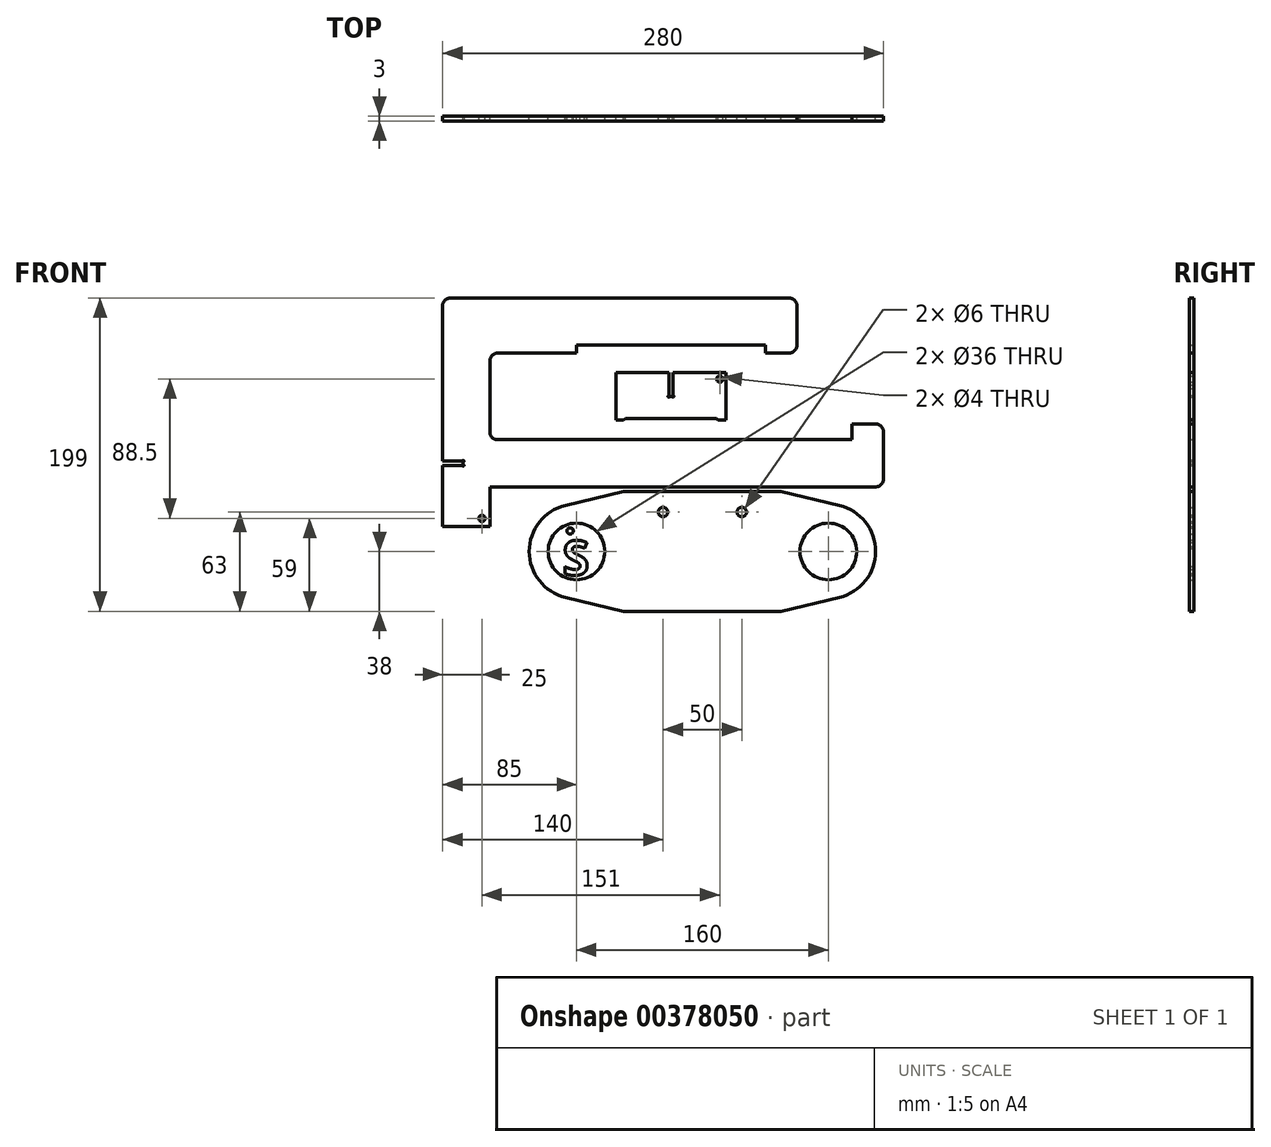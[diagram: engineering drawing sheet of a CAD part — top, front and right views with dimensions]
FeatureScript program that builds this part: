
annotation { "Feature Type Name" : "Feature", "Feature Type Description" : "" }
export const myFeature = defineFeature(function(context is Context, id is Id, definition is map)
    precondition{}
    {
        {
            var Q0;
            Q0=qCreatedBy(makeId("Front.planeOp"),FACE);
            var sketch = newSketch(context, id + "F0", { "sketchPlane" : qUnion([Q0])});
            skLineSegment(sketch, "E0", {"start": v(60, 27.5) * mm, "end": v(80, 27.5) * mm});
            skLineSegment(sketch, "E1", {"start": v(80, 27.5) * mm, "end": v(80, 62.5) * mm});
            skLineSegment(sketch, "E2", {"start": v(80, 62.5) * mm, "end": v(-145, 62.5) * mm});
            skLineSegment(sketch, "E3", {"start": v(-145, 62.5) * mm, "end": v(-145, -57.5) * mm});
            skLineSegment(sketch, "E4", {"start": v(-115, -57.5) * mm, "end": v(135, -57.5) * mm});
            skLineSegment(sketch, "E5", {"start": v(135, -57.5) * mm, "end": v(135, -17.5) * mm});
            skLineSegment(sketch, "E6", {"start": v(135, -17.5) * mm, "end": v(115, -17.5) * mm});
            skLineSegment(sketch, "E7", {"start": v(115, -17.5) * mm, "end": v(115, -27.5) * mm});
            skLineSegment(sketch, "E8", {"start": v(115, -27.5) * mm, "end": v(-115, -27.5) * mm});
            skLineSegment(sketch, "E9", {"start": v(-115, -27.5) * mm, "end": v(-115, 27.5) * mm});
            skLineSegment(sketch, "E10", {"start": v(-115, 27.5) * mm, "end": v(-60, 27.5) * mm});
            skLineSegment(sketch, "E11", {"start": v(-60, 27.5) * mm, "end": v(-60, 32.5) * mm});
            skLineSegment(sketch, "E12", {"start": v(-60, 32.5) * mm, "end": v(60, 32.5) * mm});
            skLineSegment(sketch, "E13", {"start": v(60, 32.5) * mm, "end": v(60, 27.5) * mm});
            skLineSegment(sketch, "E14", {"start": v(0, 32.5) * mm, "end": v(0, -27.5) * mm, "construction": true});
            skPoint(sketch, "E15", {"position": v(0, -27.5) * mm});
            skPoint(sketch, "E16", {"position": v(109.4, 7.93) * mm});
            skPoint(sketch, "E17", {"position": v(-115, 0) * mm});
            skLineSegment(sketch, "E18", {"start": v(-145, -57.5) * mm, "end": v(-145, -82.5) * mm});
            skLineSegment(sketch, "E19", {"start": v(-145, -82.5) * mm, "end": v(-115, -82.5) * mm});
            skLineSegment(sketch, "E20", {"start": v(-115, -82.5) * mm, "end": v(-115, -57.5) * mm});
            skCircle(sketch, "E21", {"center": v(-120, -77.5) * mm, "radius": 2 * mm});
            skSolve(sketch);
        }
        {
            var Q0;
            Q0=makeQuery(id+"F0.imprint","IMPRINT",FACE,{"disambiguationData":[TD([[makeQuery(id+"F0.imprint","IMPRINT",EDGE,{"derivedFrom":sQuery(id+"F0.wireOp",EDGE,"E0")}),1.0]])]});
            extrude(context, id + "F1", {"entities" : qUnion([Q0]), "depth" : 3 * mm, "symmetric" : true});
        }
        {
            var Q0;
            Q0=qCreatedBy(makeId("Front.planeOp"),FACE);
            var sketch = newSketch(context, id + "F2", { "sketchPlane" : qUnion([Q0])});
            skArc(sketch, "E22", {"start": v(-66.96, -69.32) * mm, "mid": v(-83.55, -79.91) * mm, "end": v(-90, -98.5) * mm});
            skArc(sketch, "E23", {"start": v(-42, -98.5) * mm, "mid": v(-60, -80.5) * mm, "end": v(-78, -98.5) * mm});
            skLineSegment(sketch, "E24", {"start": v(-66.96, -69.32) * mm, "end": v(-30, -60.5) * mm});
            skLineSegment(sketch, "E25", {"start": v(-30, -60.5) * mm, "end": v(20, -60.5) * mm});
            skLineSegment(sketch, "E26", {"start": v(165.45, -98.5) * mm, "end": v(-147.02, -98.5) * mm, "construction": true});
            skArc(sketch, "E27.MirrorCS", {"start": v(-42, -98.5) * mm, "mid": v(-60, -116.5) * mm, "end": v(-78, -98.5) * mm});
            skLineSegment(sketch, "E28.MirrorCS", {"start": v(-30, -136.5) * mm, "end": v(20, -136.5) * mm});
            skLineSegment(sketch, "E29.MirrorCS", {"start": v(-66.96, -127.68) * mm, "end": v(-30, -136.5) * mm});
            skArc(sketch, "E30.MirrorCS", {"start": v(-66.96, -127.68) * mm, "mid": v(-83.55, -117.09) * mm, "end": v(-90, -98.5) * mm});
            skLineSegment(sketch, "E31", {"start": v(20, -147.07) * mm, "end": v(20, 48.34) * mm, "construction": true});
            skArc(sketch, "E32.MirrorCS", {"start": v(82, -98.5) * mm, "mid": v(100, -116.5) * mm, "end": v(118, -98.5) * mm});
            skLineSegment(sketch, "E33.MirrorCS", {"start": v(70, -60.5) * mm, "end": v(20, -60.5) * mm});
            skLineSegment(sketch, "E34.MirrorCS", {"start": v(70, -136.5) * mm, "end": v(20, -136.5) * mm});
            skArc(sketch, "E35.MirrorCS", {"start": v(106.96, -127.68) * mm, "mid": v(123.55, -117.09) * mm, "end": v(130, -98.5) * mm});
            skArc(sketch, "E36.MirrorCS", {"start": v(82, -98.5) * mm, "mid": v(100, -80.5) * mm, "end": v(118, -98.5) * mm});
            skLineSegment(sketch, "E37.MirrorCS", {"start": v(106.96, -127.68) * mm, "end": v(70, -136.5) * mm});
            skLineSegment(sketch, "E38.MirrorCS", {"start": v(106.96, -69.32) * mm, "end": v(70, -60.5) * mm});
            skArc(sketch, "E39.MirrorCS", {"start": v(106.96, -69.32) * mm, "mid": v(123.55, -79.91) * mm, "end": v(130, -98.5) * mm});
            skCircle(sketch, "E40", {"center": v(-5, -73.5) * mm, "radius": 3 * mm});
            skCircle(sketch, "E41.MirrorC", {"center": v(45, -73.5) * mm, "radius": 3 * mm});
            skSolve(sketch);
        }
        {
            var Q0;
            Q0=makeQuery(id+"F2.imprint","IMPRINT",FACE,{"disambiguationData":[TD([[makeQuery(id+"F2.imprint","IMPRINT",EDGE,{"derivedFrom":sQuery(id+"F2.wireOp",EDGE,"E22")}),1.0]])]});
            extrude(context, id + "F3", {"entities" : qUnion([Q0]), "depth" : 3 * mm, "symmetric" : true});
        }
        {
            var Q0;
            Q0=qCreatedBy(makeId("Front.planeOp"),FACE);
            var sketch = newSketch(context, id + "F4", { "sketchPlane" : qUnion([Q0])});
            skCircle(sketch, "E42.0", {"center": v(-60, -98.5) * mm, "radius": 18 * mm, "construction": true});
            skLineSegment(sketch, "E43", {"start": v(-105.56, -98.5) * mm, "end": v(-14.37, -98.5) * mm, "construction": true});
            skLineSegment(sketch, "E44", {"start": v(-60, -105.04) * mm, "end": v(-60, -4.37) * mm, "construction": true});
            skText(sketch, "E45", { "text": "S", "fontName": "OpenSans-Bold.ttf"});
            skPoint(sketch, "E46", {"position": v(-60, -101.5) * mm});
            skCircle(sketch, "E47", {"center": v(-64, -85.5) * mm, "radius": 2 * mm});
            const initialGuessF4  = {"E45": [-0.0688, -0.1135, 1, 0, 0.022]};
            skSetInitialGuess(sketch, initialGuessF4);
            skSolve(sketch);
        }
        {
            var Q0;
            Q0=makeQuery(id+"F4.imprint","IMPRINT",FACE,{"disambiguationData":[TD([[makeQuery(id+"F4.imprint","IMPRINT",EDGE,{"derivedFrom":sQuery(id+"F4.wireOp",EDGE,"E45.sketch_text.stroke-0")}),-1.0]])]});
            extrude(context, id + "F5", {"entities" : qUnion([Q0]), "depth" : 3 * mm, "symmetric" : true});
        }
        {
            var Q0;
            Q0 = qSketchRegion(id + "F4", true);
            extrude(context, id + "F6", {"entities" : qUnion([Q0]), "operationType" : NewBodyOperationType.ADD, "depth" : 3 * mm, "symmetric" : true});
        }
        {
            var Q0;
            Q0=qCreatedBy(makeId("Front.planeOp"),FACE);
            var sketch = newSketch(context, id + "F7", { "sketchPlane" : qUnion([Q0])});
            skLineSegment(sketch, "E48.0", {"start": v(115, -27.5) * mm, "end": v(-115, -27.5) * mm, "construction": true});
            skLineSegment(sketch, "E49.0", {"start": v(-115, -57.5) * mm, "end": v(135, -57.5) * mm, "construction": true});
            skLineSegment(sketch, "E50.0", {"start": v(-145, 62.5) * mm, "end": v(-145, -82.5) * mm, "construction": true});
            skPoint(sketch, "E51.0", {"position": v(-115, -70) * mm});
            skLineSegment(sketch, "E52.0", {"start": v(-115, -82.5) * mm, "end": v(-115, -57.5) * mm, "construction": true});
            skLineSegment(sketch, "E53.0", {"start": v(-115, -27.5) * mm, "end": v(-115, 27.5) * mm, "construction": true});
            skLineSegment(sketch, "E54", {"start": v(-115, -27.5) * mm, "end": v(-115, -57.5) * mm, "construction": true});
            skLineSegment(sketch, "E55", {"start": v(-115, -42.5) * mm, "end": v(-166.9, -42.5) * mm, "construction": true});
            skLineSegment(sketch, "E56", {"start": v(-145, -42.5) * mm, "end": v(-145, -41.15) * mm});
            skLineSegment(sketch, "E57", {"start": v(-145, -41.15) * mm, "end": v(-132.5, -41.15) * mm});
            skLineSegment(sketch, "E58", {"start": v(-132, -41.65) * mm, "end": v(-132, -42.5) * mm});
            skArc(sketch, "E59", {"start": v(-132.5, -41.15) * mm, "mid": v(-131.65, -40.8) * mm, "end": v(-132, -41.65) * mm});
            skLineSegment(sketch, "E60.MirrorCS", {"start": v(-145, -43.85) * mm, "end": v(-132.5, -43.85) * mm});
            skLineSegment(sketch, "E61.MirrorCS", {"start": v(-132, -43.35) * mm, "end": v(-132, -42.5) * mm});
            skArc(sketch, "E62.MirrorCS", {"start": v(-132.5, -43.85) * mm, "mid": v(-131.65, -44.2) * mm, "end": v(-132, -43.35) * mm});
            skLineSegment(sketch, "E63", {"start": v(-145, -41.15) * mm, "end": v(-145, -43.85) * mm});
            skSolve(sketch);
        }
        {
            var Q0;
            Q0 = qSketchRegion(id + "F7", true);
            extrude(context, id + "F8", {"entities" : qUnion([Q0]), "operationType" : NewBodyOperationType.REMOVE, "oppositeDirection" : true, "depth" : 25 * mm, "symmetric" : true});
        }
        {
            var Q0;
            Q0=qCreatedBy(makeId("Front.planeOp"),FACE);
            var sketch = newSketch(context, id + "F9", { "sketchPlane" : qUnion([Q0])});
            skLineSegment(sketch, "E64.bottom", {"start": v(-35, -15) * mm, "end": v(-30, -15) * mm});
            skLineSegment(sketch, "E64.top", {"start": v(-35, 15) * mm, "end": v(-1.35, 15) * mm});
            skLineSegment(sketch, "E64.left", {"start": v(-35, -15) * mm, "end": v(-35, 15) * mm});
            skLineSegment(sketch, "E64.right", {"start": v(35, -15) * mm, "end": v(35, 15) * mm});
            skPoint(sketch, "E64.middle", {"position": v(0, 0) * mm});
            skLineSegment(sketch, "E65", {"start": v(-1.35, 15) * mm, "end": v(-1.35, 7.2) * mm});
            skLineSegment(sketch, "E66", {"start": v(-0.85, 0) * mm, "end": v(0, 0) * mm});
            skArc(sketch, "E67", {"start": v(-0.85, 0) * mm, "mid": v(-1.7, -0.35) * mm, "end": v(-1.35, 0.5) * mm});
            skLineSegment(sketch, "E68", {"start": v(0, 22.78) * mm, "end": v(0, -12.8) * mm, "construction": true});
            skLineSegment(sketch, "E69", {"start": v(-1.35, 5) * mm, "end": v(-1.25, 5.1) * mm});
            skLineSegment(sketch, "E70", {"start": v(-1.25, 5.1) * mm, "end": v(-1.25, 7.1) * mm});
            skLineSegment(sketch, "E71", {"start": v(-1.25, 7.1) * mm, "end": v(-1.35, 7.2) * mm});
            skLineSegment(sketch, "E72.trimOffspring", {"start": v(-1.35, 5) * mm, "end": v(-1.35, 0.5) * mm});
            skPoint(sketch, "E73.orphan", {"position": v(-1.35, 15) * mm});
            skLineSegment(sketch, "E74.MirrorCS", {"start": v(1.25, 7.1) * mm, "end": v(1.35, 7.2) * mm});
            skArc(sketch, "E75.MirrorCS", {"start": v(0.85, 0) * mm, "mid": v(1.7, -0.35) * mm, "end": v(1.35, 0.5) * mm});
            skLineSegment(sketch, "E76.MirrorCS", {"start": v(1.35, 5) * mm, "end": v(1.25, 5.1) * mm});
            skLineSegment(sketch, "E77.MirrorCS", {"start": v(0.85, 0) * mm, "end": v(0, 0) * mm});
            skLineSegment(sketch, "E78.MirrorCS", {"start": v(1.25, 5.1) * mm, "end": v(1.25, 7.1) * mm});
            skPoint(sketch, "E79.MirrorP", {"position": v(1.35, 15) * mm});
            skLineSegment(sketch, "E80.MirrorCS", {"start": v(1.35, 15) * mm, "end": v(1.35, 7.2) * mm});
            skLineSegment(sketch, "E81.MirrorCS", {"start": v(1.35, 5) * mm, "end": v(1.35, 0.5) * mm});
            skLineSegment(sketch, "E82", {"start": v(1.35, 15) * mm, "end": v(35, 15) * mm});
            skLineSegment(sketch, "E83", {"start": v(-30, -15) * mm, "end": v(-29, -14) * mm});
            skLineSegment(sketch, "E84", {"start": v(-29, -14) * mm, "end": v(0, -14) * mm});
            skLineSegment(sketch, "E85.MirrorCS", {"start": v(29, -14) * mm, "end": v(0, -14) * mm});
            skLineSegment(sketch, "E86.MirrorCS", {"start": v(35, -15) * mm, "end": v(30, -15) * mm});
            skLineSegment(sketch, "E87.MirrorCS", {"start": v(30, -15) * mm, "end": v(29, -14) * mm});
            skCircle(sketch, "E88", {"center": v(31, 11) * mm, "radius": 2 * mm});
            skSolve(sketch);
        }
        {
            var Q0;
            Q0 = qSketchRegion(id + "F9", true);
            extrude(context, id + "F10", {"entities" : qUnion([Q0]), "depth" : 3 * mm, "symmetric" : true});
        }
        {
            var Q0;
            Q0=makeQuery(id+"F1.opExtrude","SWEPT_EDGE",EDGE,{"disambiguationData":[OSD([sQuery(id+"F0.wireOp",EDGE,"E2"),sQuery(id+"F0.wireOp",EDGE,"E3")])]});
            var Q1;
            Q1=makeQuery(id+"F1.opExtrude","SWEPT_EDGE",EDGE,{"disambiguationData":[OSD([sQuery(id+"F0.wireOp",EDGE,"E1"),sQuery(id+"F0.wireOp",EDGE,"E2")])]});
            var Q2;
            Q2=makeQuery(id+"F1.opExtrude","SWEPT_EDGE",EDGE,{"disambiguationData":[OSD([sQuery(id+"F0.wireOp",EDGE,"E0"),sQuery(id+"F0.wireOp",EDGE,"E1")])]});
            var Q3;
            Q3=makeQuery(id+"F1.opExtrude","SWEPT_EDGE",EDGE,{"disambiguationData":[OSD([sQuery(id+"F0.wireOp",EDGE,"E5"),sQuery(id+"F0.wireOp",EDGE,"E6")])]});
            var Q4;
            Q4=makeQuery(id+"F1.opExtrude","SWEPT_EDGE",EDGE,{"disambiguationData":[OSD([sQuery(id+"F0.wireOp",EDGE,"E4"),sQuery(id+"F0.wireOp",EDGE,"E5")])]});
            var Q5;
            Q5=makeQuery(id+"F1.opExtrude","SWEPT_EDGE",EDGE,{"disambiguationData":[OSD([sQuery(id+"F0.wireOp",EDGE,"E8"),sQuery(id+"F0.wireOp",EDGE,"E9")])]});
            var Q6;
            Q6=makeQuery(id+"F1.opExtrude","SWEPT_EDGE",EDGE,{"disambiguationData":[OSD([sQuery(id+"F0.wireOp",EDGE,"E9"),sQuery(id+"F0.wireOp",EDGE,"E10")])]});
            fillet(context, id + "F11", {"entities" : qUnion([Q0, Q1, Q2, Q3, Q4, Q5, Q6]), "radius" : 5 * mm, "tangentPropagation" : true, "allowEdgeOverflow" : false});
        }
    });
